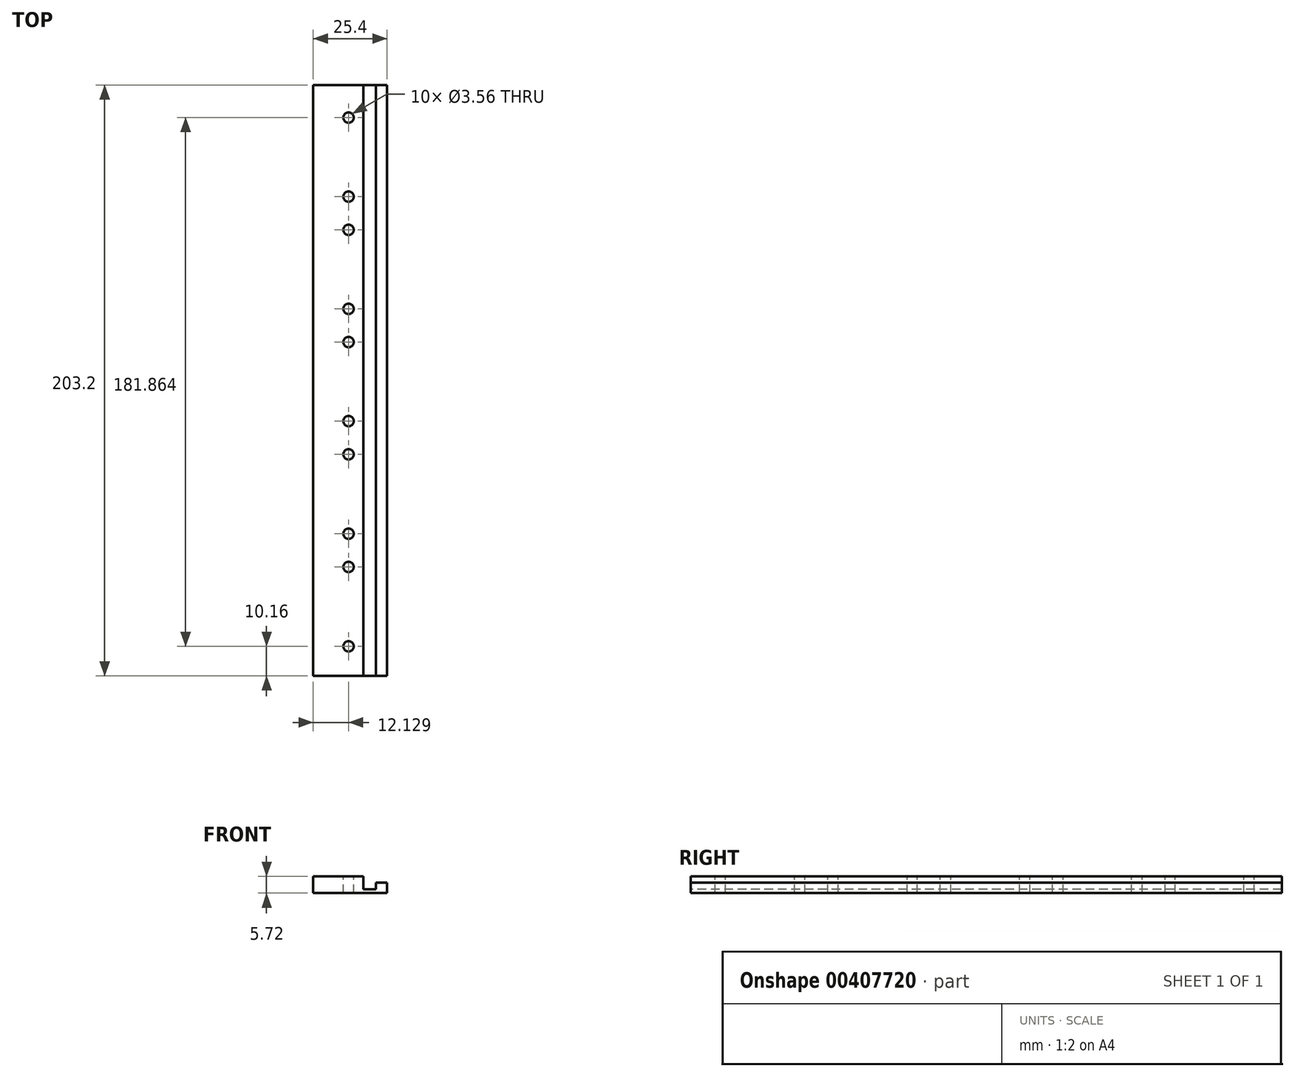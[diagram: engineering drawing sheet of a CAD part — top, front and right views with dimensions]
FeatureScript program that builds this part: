
annotation { "Feature Type Name" : "Feature", "Feature Type Description" : "" }
export const myFeature = defineFeature(function(context is Context, id is Id, definition is map)
    precondition{}
    {
        {
            var Q0;
            Q0=qCreatedBy(makeId("Top.planeOp"),FACE);
            var sketch = newSketch(context, id + "F0", { "sketchPlane" : qUnion([Q0])});
            skLineSegment(sketch, "E0.bottom", {"start": v(0, 0) * mm, "end": v(25.4, 0) * mm});
            skLineSegment(sketch, "E0.top", {"start": v(0, 203.2) * mm, "end": v(25.4, 203.2) * mm});
            skLineSegment(sketch, "E0.left", {"start": v(0, 0) * mm, "end": v(0, 203.2) * mm});
            skLineSegment(sketch, "E0.right", {"start": v(25.4, 0) * mm, "end": v(25.4, 203.2) * mm});
            skSolve(sketch);
        }
        {
            var Q0;
            Q0 = qSketchRegion(id + "F0", true);
            extrude(context, id + "F1", {"entities" : qUnion([Q0]), "depth" : 5.7 * mm});
        }
        {
            var Q0;
            Q0=makeQuery(id+"F1.opExtrude","CAP_FACE",FACE,{"disambiguationData":[OSD([sQuery(id+"F0.wireOp",EDGE,"E0.bottom"),sQuery(id+"F0.wireOp",EDGE,"E0.top"),sQuery(id+"F0.wireOp",EDGE,"E0.left"),sQuery(id+"F0.wireOp",EDGE,"E0.right")])],"isStart":false});
            var sketch = newSketch(context, id + "F2", { "sketchPlane" : qUnion([Q0])});
            skLineSegment(sketch, "E1.bottom", {"start": v(17.2, 203.2) * mm, "end": v(21.59, 203.2) * mm});
            skLineSegment(sketch, "E1.top", {"start": v(17.2, 0) * mm, "end": v(21.59, 0) * mm});
            skLineSegment(sketch, "E1.left", {"start": v(17.2, 203.2) * mm, "end": v(17.2, 0) * mm});
            skLineSegment(sketch, "E1.right", {"start": v(21.59, 203.2) * mm, "end": v(21.59, 0) * mm});
            skSolve(sketch);
        }
        {
            var Q0;
            Q0 = qSketchRegion(id + "F2", true);
            extrude(context, id + "F3", {"entities" : qUnion([Q0]), "operationType" : NewBodyOperationType.REMOVE, "oppositeDirection" : true, "depth" : 4.44 * mm});
        }
        {
            var Q0;
            {var subQ0=sQuery(id+"F0.wireOp",EDGE,"E0.bottom");var subQ1=sQuery(id+"F0.wireOp",EDGE,"E0.top");var subQ2=sQuery(id+"F0.wireOp",EDGE,"E0.left");Q0=makeQuery(id+"F3.boolean.opBoolean","SPLIT",FACE,{"disambiguationData":[TD([makeQuery(id+"F1.opExtrude","SWEPT_FACE",FACE,{"disambiguationData":[OSD([subQ2])]})])],"derivedFrom":makeQuery(id+"F1.opExtrude","CAP_FACE",FACE,{"disambiguationData":[OSD([subQ0,subQ1,subQ2,sQuery(id+"F0.wireOp",EDGE,"E0.right")])],"isStart":false})});}
            var sketch = newSketch(context, id + "F4", { "sketchPlane" : qUnion([Q0])});
            skLineSegment(sketch, "E2.bottom", {"start": v(19.68, 210.45) * mm, "end": v(42.14, 210.45) * mm});
            skLineSegment(sketch, "E2.top", {"start": v(19.68, -28.58) * mm, "end": v(42.14, -28.58) * mm});
            skLineSegment(sketch, "E2.left", {"start": v(19.68, 210.45) * mm, "end": v(19.68, -28.58) * mm});
            skLineSegment(sketch, "E2.right", {"start": v(42.14, 210.45) * mm, "end": v(42.14, -28.58) * mm});
            skSolve(sketch);
        }
        {
            var Q0;
            Q0 = qSketchRegion(id + "F4", true);
            extrude(context, id + "F5", {"entities" : qUnion([Q0]), "operationType" : NewBodyOperationType.REMOVE, "oppositeDirection" : true, "depth" : 2.08 * mm});
        }
        {
            var Q0;
            {var subQ0=sQuery(id+"F0.wireOp",EDGE,"E0.bottom");var subQ1=sQuery(id+"F0.wireOp",EDGE,"E0.top");var subQ2=sQuery(id+"F0.wireOp",EDGE,"E0.left");Q0=makeQuery(id+"F3.boolean.opBoolean","SPLIT",FACE,{"disambiguationData":[TD([makeQuery(id+"F1.opExtrude","SWEPT_FACE",FACE,{"disambiguationData":[OSD([subQ2])]})])],"derivedFrom":makeQuery(id+"F1.opExtrude","CAP_FACE",FACE,{"disambiguationData":[OSD([subQ0,subQ1,subQ2,sQuery(id+"F0.wireOp",EDGE,"E0.right")])],"isStart":false})});}
            var sketch = newSketch(context, id + "F6", { "sketchPlane" : qUnion([Q0])});
            skCircle(sketch, "E3", {"center": v(12.13, 37.47) * mm, "radius": 1.78 * mm});
            skCircle(sketch, "E4", {"center": v(12.13, 10.16) * mm, "radius": 1.78 * mm});
            skCircle(sketch, "E5", {"center": v(12.13, 48.9) * mm, "radius": 1.78 * mm});
            skLineSegment(sketch, "E6", {"start": v(0, 62.55) * mm, "end": v(17.2, 62.55) * mm, "construction": true});
            skCircle(sketch, "E7.MirrorC", {"center": v(12.13, 87.63) * mm, "radius": 1.78 * mm});
            skCircle(sketch, "E8.MirrorC", {"center": v(12.13, 76.2) * mm, "radius": 1.78 * mm});
            skCircle(sketch, "E9.0.1.0", {"center": v(12.13, 114.8) * mm, "radius": 1.78 * mm});
            skCircle(sketch, "E9.0.1.1", {"center": v(12.13, 126.24) * mm, "radius": 1.78 * mm});
            skCircle(sketch, "E9.0.2.0", {"center": v(12.13, 153.42) * mm, "radius": 1.78 * mm});
            skCircle(sketch, "E9.0.2.1", {"center": v(12.13, 164.85) * mm, "radius": 1.78 * mm});
            skCircle(sketch, "E9.0.3.0", {"center": v(12.13, 192.02) * mm, "radius": 1.78 * mm});
            skLineSegment(sketch, "E9.direction1", {"start": v(12.13, 76.2) * mm, "end": v(38.8, 76.2) * mm, "construction": true});
            skLineSegment(sketch, "E9.direction2", {"start": v(12.13, 76.2) * mm, "end": v(12.13, 114.8) * mm, "construction": true});
            skSolve(sketch);
        }
        {
            var Q0;
            Q0 = qSketchRegion(id + "F6", true);
            extrude(context, id + "F7", {"entities" : qUnion([Q0]), "operationType" : NewBodyOperationType.REMOVE, "oppositeDirection" : true, "depth" : 25.4 * mm});
        }
    });
